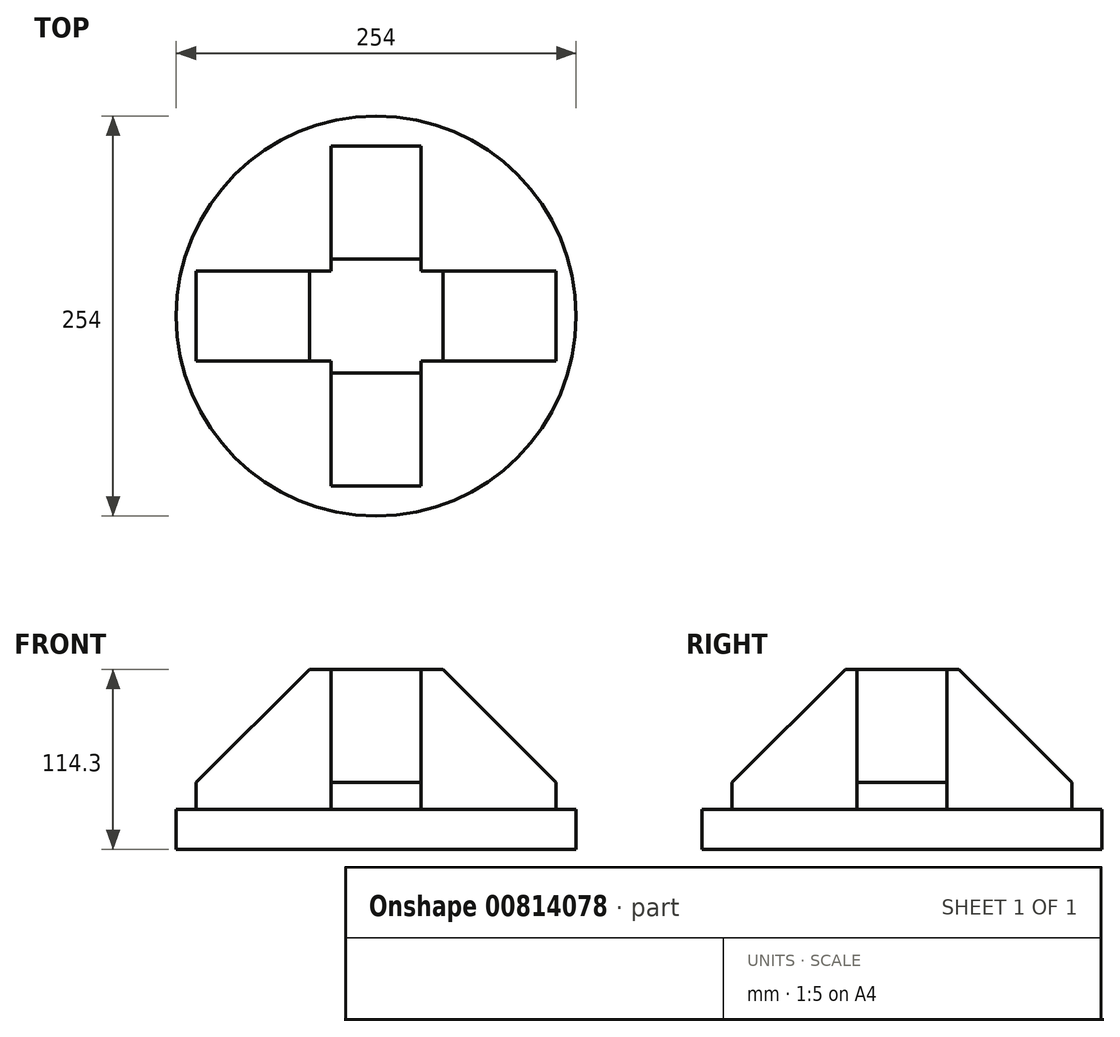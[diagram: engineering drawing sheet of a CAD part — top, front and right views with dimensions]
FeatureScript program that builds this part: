
annotation { "Feature Type Name" : "Feature", "Feature Type Description" : "" }
export const myFeature = defineFeature(function(context is Context, id is Id, definition is map)
    precondition{}
    {
        {
            var Q0;
            Q0=qCreatedBy(makeId("Top.planeOp"),FACE);
            var sketch = newSketch(context, id + "F0", { "sketchPlane" : qUnion([Q0])});
            skCircle(sketch, "E0", {"center": v(0, 0) * mm, "radius": 127 * mm});
            skSolve(sketch);
        }
        {
            var Q0;
            Q0=makeQuery(id+"F0.imprint","IMPRINT",FACE,{"disambiguationData":[TD([[makeQuery(id+"F0.imprint","IMPRINT",EDGE,{"derivedFrom":sQuery(id+"F0.wireOp",EDGE,"E0")}),1.0]])]});
            extrude(context, id + "F1", {"entities" : qUnion([Q0]), "depth" : 25.4 * mm, "offsetDistance" : 25.4 * mm});
        }
        {
            var Q0;
            Q0=qCreatedBy(makeId("Right.planeOp"),FACE);
            var sketch = newSketch(context, id + "F2", { "sketchPlane" : qUnion([Q0])});
            skLineSegment(sketch, "E1", {"start": v(-107.95, 25.4) * mm, "end": v(-107.95, 42.46) * mm});
            skLineSegment(sketch, "E2", {"start": v(-107.95, 42.46) * mm, "end": v(-36.1, 114.3) * mm});
            skLineSegment(sketch, "E3", {"start": v(-36.1, 114.3) * mm, "end": v(0, 114.3) * mm});
            skLineSegment(sketch, "E4", {"start": v(0, 114.3) * mm, "end": v(0, 25.4) * mm});
            skLineSegment(sketch, "E5", {"start": v(0, 25.4) * mm, "end": v(-107.95, 25.4) * mm});
            skLineSegment(sketch, "E6", {"start": v(0, 0) * mm, "end": v(0, 105.86) * mm, "construction": true});
            skPoint(sketch, "E6.endSnap0", {"position": v(0, 69.85) * mm});
            skLineSegment(sketch, "E7.MirrorCS", {"start": v(107.95, 25.4) * mm, "end": v(107.95, 42.46) * mm});
            skLineSegment(sketch, "E8.MirrorCS", {"start": v(36.1, 114.3) * mm, "end": v(0, 114.3) * mm});
            skLineSegment(sketch, "E9.MirrorCS", {"start": v(0, 25.4) * mm, "end": v(107.95, 25.4) * mm});
            skLineSegment(sketch, "E10.MirrorCS", {"start": v(107.95, 42.46) * mm, "end": v(36.1, 114.3) * mm});
            skSolve(sketch);
        }
        {
            var Q0;
            Q0 = qSketchRegion(id + "F2", true);
            extrude(context, id + "F3", {"entities" : qUnion([Q0]), "operationType" : NewBodyOperationType.ADD, "endBound" : BoundingType.SYMMETRIC, "depth" : 57.15 * mm, "offsetDistance" : 25.4 * mm});
        }
        {
            var Q0;
            Q0=qCreatedBy(makeId("Front.planeOp"),FACE);
            var sketch = newSketch(context, id + "F4", { "sketchPlane" : qUnion([Q0])});
            skLineSegment(sketch, "E11", {"start": v(-114.3, 25.4) * mm, "end": v(-114.3, 42.46) * mm});
            skLineSegment(sketch, "E12", {"start": v(-114.3, 42.46) * mm, "end": v(-42.46, 114.3) * mm});
            skLineSegment(sketch, "E13", {"start": v(-42.46, 114.3) * mm, "end": v(0, 114.3) * mm});
            skLineSegment(sketch, "E14", {"start": v(0, 114.3) * mm, "end": v(0, 25.4) * mm});
            skLineSegment(sketch, "E15", {"start": v(0, 25.4) * mm, "end": v(-114.3, 25.4) * mm});
            skLineSegment(sketch, "E16", {"start": v(0, 0) * mm, "end": v(0, 124.28) * mm, "construction": true});
            skLineSegment(sketch, "E17.MirrorCS", {"start": v(114.3, 25.4) * mm, "end": v(114.3, 42.46) * mm});
            skLineSegment(sketch, "E18.MirrorCS", {"start": v(114.3, 42.46) * mm, "end": v(42.46, 114.3) * mm});
            skLineSegment(sketch, "E19.MirrorCS", {"start": v(0, 25.4) * mm, "end": v(114.3, 25.4) * mm});
            skLineSegment(sketch, "E20.MirrorCS", {"start": v(42.46, 114.3) * mm, "end": v(0, 114.3) * mm});
            skSolve(sketch);
        }
        {
            var Q0;
            Q0 = qSketchRegion(id + "F4", true);
            extrude(context, id + "F5", {"entities" : qUnion([Q0]), "operationType" : NewBodyOperationType.ADD, "endBound" : BoundingType.SYMMETRIC, "oppositeDirection" : true, "depth" : 57.15 * mm, "offsetDistance" : 25.4 * mm});
        }
    });
